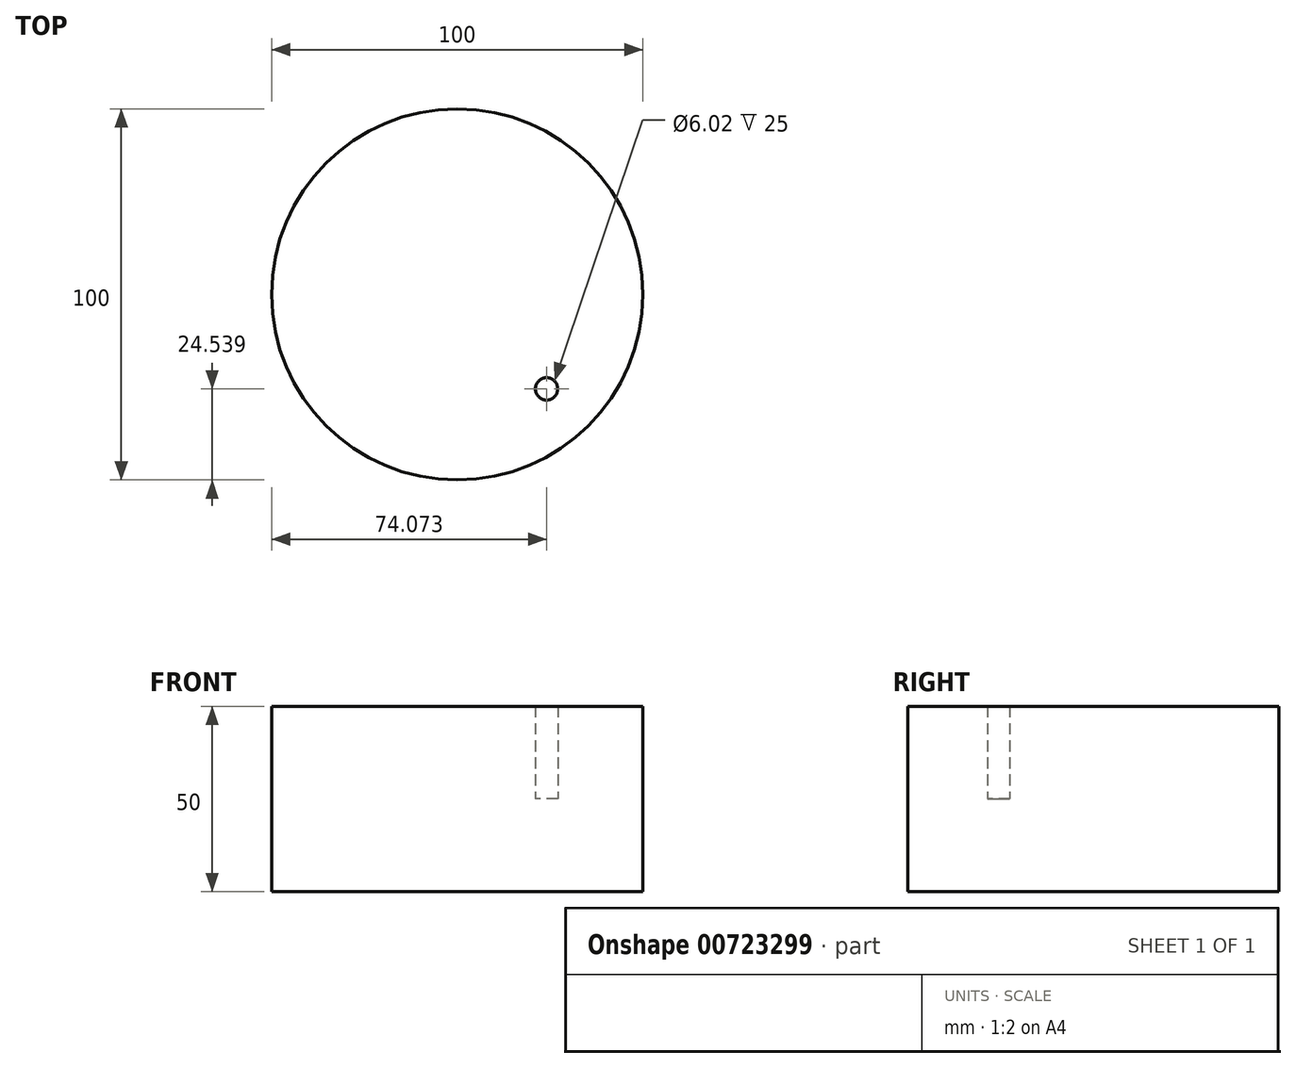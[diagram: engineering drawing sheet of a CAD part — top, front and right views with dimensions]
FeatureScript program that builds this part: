
annotation { "Feature Type Name" : "Feature", "Feature Type Description" : "" }
export const myFeature = defineFeature(function(context is Context, id is Id, definition is map)
    precondition{}
    {
        {
            var Q0;
            Q0=qCreatedBy(makeId("Top.planeOp"),FACE);
            var sketch = newSketch(context, id + "F0", { "sketchPlane" : qUnion([Q0])});
            skCircle(sketch, "E0", {"center": v(0, 0) * mm, "radius": 50 * mm});
            skSolve(sketch);
        }
        {
            var Q0;
            Q0=makeQuery(id+"F0.imprint","IMPRINT",FACE,{"disambiguationData":[TD([[makeQuery(id+"F0.imprint","IMPRINT",EDGE,{"derivedFrom":sQuery(id+"F0.wireOp",EDGE,"E0")}),1.0]])]});
            extrude(context, id + "F1", {"entities" : qUnion([Q0]), "depth" : 25 * mm, "offsetDistance" : 25 * mm});
        }
        {
            var Q0;
            Q0=makeQuery(id+"F1.opExtrude","CAP_FACE",FACE,{"disambiguationData":[OSD([sQuery(id+"F0.wireOp",EDGE,"E0")])],"isStart":false});
            var sketch = newSketch(context, id + "F2", { "sketchPlane" : qUnion([Q0])});
            skCircle(sketch, "E1.cCircle", {"center": v(0, 0) * mm, "radius": 20.02 * mm, "construction": true});
            skLineSegment(sketch, "E1.0", {"start": v(-20.47, 10.74) * mm, "end": v(-0.93, 23.1) * mm});
            skLineSegment(sketch, "E1.1", {"start": v(-0.93, 23.1) * mm, "end": v(19.53, 12.36) * mm});
            skLineSegment(sketch, "E1.2", {"start": v(19.53, 12.36) * mm, "end": v(20.47, -10.74) * mm});
            skLineSegment(sketch, "E1.3", {"start": v(20.47, -10.74) * mm, "end": v(0.93, -23.1) * mm});
            skLineSegment(sketch, "E1.4", {"start": v(0.93, -23.1) * mm, "end": v(-19.53, -12.36) * mm});
            skLineSegment(sketch, "E1.5", {"start": v(-19.53, -12.36) * mm, "end": v(-20.47, 10.74) * mm});
            skPoint(sketch, "E1.0.midPoint", {"position": v(-10.7, 16.92) * mm});
            skSolve(sketch);
        }
        {
            var Q0;
            Q0=makeQuery(id+"F2.imprint","IMPRINT",FACE,{"disambiguationData":[TD([[makeQuery(id+"F2.imprint","IMPRINT",EDGE,{"derivedFrom":sQuery(id+"F2.wireOp",EDGE,"E1.0")}),-1.0]])]});
            extrude(context, id + "F3", {"entities" : qUnion([Q0]), "operationType" : NewBodyOperationType.ADD, "depth" : 25 * mm, "offsetDistance" : 25 * mm});
        }
        {
            var Q0;
            Q0=makeQuery(id+"F1.opExtrude","CAP_FACE",FACE,{"disambiguationData":[OSD([sQuery(id+"F0.wireOp",EDGE,"E0")])],"isStart":false});
            var sketch = newSketch(context, id + "F4", { "sketchPlane" : qUnion([Q0])});
            skCircle(sketch, "E2", {"center": v(24.07, -25.46) * mm, "radius": 3 * mm});
            skSolve(sketch);
        }
        {
            var Q0;
            Q0=makeQuery(id+"F4.imprint","IMPRINT",FACE,{"disambiguationData":[TD([[makeQuery(id+"F4.imprint","IMPRINT",EDGE,{"derivedFrom":sQuery(id+"F4.wireOp",EDGE,"E2")}),-1.0]])]});
            extrude(context, id + "F5", {"entities" : qUnion([Q0]), "operationType" : NewBodyOperationType.ADD, "depth" : 25 * mm, "offsetDistance" : 25 * mm});
        }
    });
